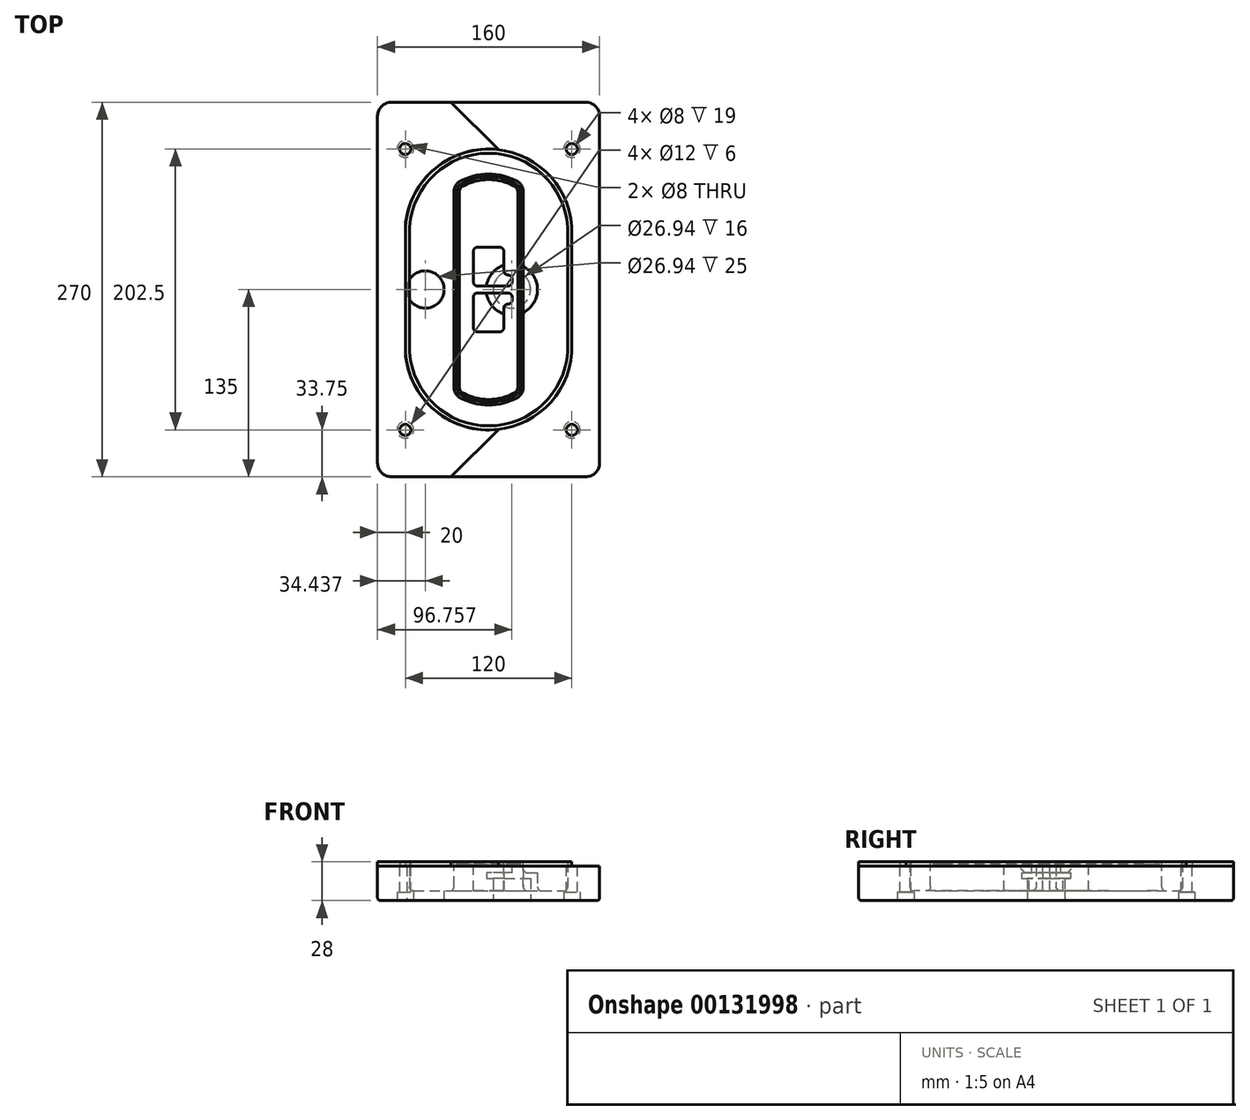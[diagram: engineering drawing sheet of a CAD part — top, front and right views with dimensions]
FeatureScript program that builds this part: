
annotation { "Feature Type Name" : "Feature", "Feature Type Description" : "" }
export const myFeature = defineFeature(function(context is Context, id is Id, definition is map)
    precondition{}
    {
        {
            var Q0;
            Q0=qCreatedBy(makeId("Top.planeOp"),FACE);
            var sketch = newSketch(context, id + "F0", { "sketchPlane" : qUnion([Q0])});
            skPoint(sketch, "E0.rect.middle", {"position": v(0, 0) * mm});
            skLineSegment(sketch, "E1.bottom", {"start": v(-70, -135) * mm, "end": v(70, -135) * mm});
            skLineSegment(sketch, "E1.top", {"start": v(-70, 135) * mm, "end": v(70, 135) * mm});
            skLineSegment(sketch, "E1.left", {"start": v(-80, -125) * mm, "end": v(-80, 125) * mm});
            skLineSegment(sketch, "E1.right", {"start": v(80, -125) * mm, "end": v(80, 125) * mm});
            skLineSegment(sketch, "E2", {"start": v(-80, 135) * mm, "end": v(80, -135) * mm, "construction": true});
            skLineSegment(sketch, "E3", {"start": v(80, 135) * mm, "end": v(-80, -135) * mm, "construction": true});
            skCircle(sketch, "E4", {"center": v(-60, 101.25) * mm, "radius": 4 * mm});
            skCircle(sketch, "E5", {"center": v(60, 101.25) * mm, "radius": 4 * mm});
            skCircle(sketch, "E6", {"center": v(60, -101.25) * mm, "radius": 4 * mm});
            skCircle(sketch, "E7", {"center": v(-60, -101.25) * mm, "radius": 4 * mm});
            skLineSegment(sketch, "E8", {"start": v(-60, 101.25) * mm, "end": v(60, 101.25) * mm, "construction": true});
            skLineSegment(sketch, "E9", {"start": v(60, 101.25) * mm, "end": v(60, -101.25) * mm, "construction": true});
            skLineSegment(sketch, "E10", {"start": v(60, -101.25) * mm, "end": v(-60, -101.25) * mm, "construction": true});
            skLineSegment(sketch, "E11", {"start": v(-60, -101.25) * mm, "end": v(-60, 101.25) * mm, "construction": true});
            skLineSegment(sketch, "E12", {"start": v(-60, 44.66) * mm, "end": v(-60, -44.66) * mm});
            skLineSegment(sketch, "E13", {"start": v(60, 44.66) * mm, "end": v(60, -44.66) * mm});
            skArc(sketch, "E14", {"start": v(59.98, 45.37) * mm, "mid": v(0, 101.25) * mm, "end": v(-59.98, 45.37) * mm});
            skArc(sketch, "E15", {"start": v(-59.98, -45.37) * mm, "mid": v(0, -101.25) * mm, "end": v(59.98, -45.37) * mm});
            skLineSegment(sketch, "E16", {"start": v(-60, 0) * mm, "end": v(60, 0) * mm, "construction": true});
            skPoint(sketch, "E17.visualSharp", {"position": v(-60, -45) * mm});
            skArc(sketch, "E17.filletArc", {"start": v(-60, -44.66) * mm, "mid": v(-60, -45.02) * mm, "end": v(-59.98, -45.37) * mm});
            skPoint(sketch, "E18.visualSharp", {"position": v(-60, 45) * mm});
            skArc(sketch, "E18.filletArc", {"start": v(-59.98, 45.37) * mm, "mid": v(-60, 45.02) * mm, "end": v(-60, 44.66) * mm});
            skPoint(sketch, "E19.visualSharp", {"position": v(60, 45) * mm});
            skArc(sketch, "E19.filletArc", {"start": v(60, 44.66) * mm, "mid": v(60, 45.02) * mm, "end": v(59.98, 45.37) * mm});
            skPoint(sketch, "E20.visualSharp", {"position": v(60, -45) * mm});
            skArc(sketch, "E20.filletArc", {"start": v(59.98, -45.37) * mm, "mid": v(60, -45.02) * mm, "end": v(60, -44.66) * mm});
            skPoint(sketch, "E21.visualSharp", {"position": v(-80, 135) * mm});
            skArc(sketch, "E21.filletArc", {"start": v(-70, 135) * mm, "mid": v(-77.07, 132.07) * mm, "end": v(-80, 125) * mm});
            skPoint(sketch, "E22.visualSharp", {"position": v(80, 135) * mm});
            skArc(sketch, "E22.filletArc", {"start": v(80, 125) * mm, "mid": v(77.07, 132.07) * mm, "end": v(70, 135) * mm});
            skPoint(sketch, "E23.visualSharp", {"position": v(80, -135) * mm});
            skArc(sketch, "E23.filletArc", {"start": v(70, -135) * mm, "mid": v(77.07, -132.07) * mm, "end": v(80, -125) * mm});
            skPoint(sketch, "E24.visualSharp", {"position": v(-80, -135) * mm});
            skArc(sketch, "E24.filletArc", {"start": v(-80, -125) * mm, "mid": v(-77.07, -132.07) * mm, "end": v(-70, -135) * mm});
            skArc(sketch, "E25.0", {"start": v(57, 44.66) * mm, "mid": v(57, 44.9) * mm, "end": v(56.98, 45.16) * mm});
            skLineSegment(sketch, "E25.1", {"start": v(57, 44.66) * mm, "end": v(57, -44.66) * mm});
            skArc(sketch, "E25.2", {"start": v(56.98, -45.16) * mm, "mid": v(57, -44.9) * mm, "end": v(57, -44.66) * mm});
            skArc(sketch, "E25.3", {"start": v(-56.98, -45.16) * mm, "mid": v(0, -98.25) * mm, "end": v(56.98, -45.16) * mm});
            skArc(sketch, "E25.4", {"start": v(-57, -44.66) * mm, "mid": v(-57, -44.9) * mm, "end": v(-56.98, -45.16) * mm});
            skArc(sketch, "E25.5", {"start": v(56.98, 45.16) * mm, "mid": v(0, 98.25) * mm, "end": v(-56.98, 45.16) * mm});
            skLineSegment(sketch, "E25.6", {"start": v(-57, 44.66) * mm, "end": v(-57, -44.66) * mm});
            skArc(sketch, "E25.7", {"start": v(-56.98, 45.16) * mm, "mid": v(-57, 44.9) * mm, "end": v(-57, 44.66) * mm});
            skArc(sketch, "E26.0", {"start": v(-63.97, 45.65) * mm, "mid": v(-64, 45.16) * mm, "end": v(-64, 44.66) * mm});
            skArc(sketch, "E26.1", {"start": v(63.97, 45.65) * mm, "mid": v(0, 105.25) * mm, "end": v(-63.97, 45.65) * mm});
            skArc(sketch, "E26.2", {"start": v(64, 44.66) * mm, "mid": v(64, 45.16) * mm, "end": v(63.97, 45.65) * mm});
            skLineSegment(sketch, "E26.3", {"start": v(64, 44.66) * mm, "end": v(64, -44.66) * mm});
            skArc(sketch, "E26.4", {"start": v(63.97, -45.65) * mm, "mid": v(64, -45.16) * mm, "end": v(64, -44.66) * mm});
            skLineSegment(sketch, "E26.5", {"start": v(-64, 44.66) * mm, "end": v(-64, -44.66) * mm});
            skArc(sketch, "E26.6", {"start": v(-63.97, -45.65) * mm, "mid": v(0, -105.25) * mm, "end": v(63.97, -45.65) * mm});
            skArc(sketch, "E26.7", {"start": v(-64, -44.66) * mm, "mid": v(-64, -45.16) * mm, "end": v(-63.97, -45.65) * mm});
            skSolve(sketch);
        }
        {
            var Q0;
            Q0=makeQuery(id+"F0.imprint","IMPRINT",FACE,{"disambiguationData":[TD([[makeQuery(id+"F0.imprint","IMPRINT",EDGE,{"derivedFrom":sQuery(id+"F0.wireOp",EDGE,"E1.bottom")}),1.0]])]});
            var Q1;
            Q1=makeQuery(id+"F0.imprint","IMPRINT",FACE,{"disambiguationData":[TD([[makeQuery(id+"F0.imprint","IMPRINT",EDGE,{"derivedFrom":sQuery(id+"F0.wireOp",EDGE,"E12")}),1.0]])]});
            var Q2;
            Q2=makeQuery(id+"F0.imprint","IMPRINT",FACE,{"disambiguationData":[TD([[makeQuery(id+"F0.imprint","IMPRINT",EDGE,{"derivedFrom":sQuery(id+"F0.wireOp",EDGE,"E25.0")}),1.0]])]});
            var Q3;
            Q3=makeQuery(id+"F0.imprint","IMPRINT",FACE,{"disambiguationData":[TD([[makeQuery(id+"F0.imprint","IMPRINT",EDGE,{"derivedFrom":sQuery(id+"F0.wireOp",EDGE,"E12")}),-1.0]])]});
            extrude(context, id + "F1", {"entities" : qUnion([Q0, Q1, Q2, Q3]), "oppositeDirection" : true, "depth" : 25 * mm});
        }
        {
            var Q0;
            Q0=makeQuery(id+"F0.imprint","IMPRINT",FACE,{"disambiguationData":[TD([[makeQuery(id+"F0.imprint","IMPRINT",EDGE,{"derivedFrom":sQuery(id+"F0.wireOp",EDGE,"E12")}),1.0]])]});
            extrude(context, id + "F2", {"entities" : qUnion([Q0]), "operationType" : NewBodyOperationType.ADD, "depth" : 3 * mm});
        }
        {
            var Q0;
            Q0=makeQuery(id+"F0.imprint","IMPRINT",FACE,{"disambiguationData":[TD([[makeQuery(id+"F0.imprint","IMPRINT",EDGE,{"derivedFrom":sQuery(id+"F0.wireOp",EDGE,"E25.0")}),1.0]])]});
            extrude(context, id + "F3", {"entities" : qUnion([Q0]), "operationType" : NewBodyOperationType.REMOVE, "oppositeDirection" : true, "depth" : 18 * mm});
        }
        {
            var Q0;
            Q0=makeQuery(id+"F2.opExtrude","CAP_FACE",FACE,{"disambiguationData":[OSD([sQuery(id+"F0.wireOp",EDGE,"E12"),sQuery(id+"F0.wireOp",EDGE,"E13"),sQuery(id+"F0.wireOp",EDGE,"E14"),sQuery(id+"F0.wireOp",EDGE,"E15"),sQuery(id+"F0.wireOp",EDGE,"E17.filletArc"),sQuery(id+"F0.wireOp",EDGE,"E18.filletArc"),sQuery(id+"F0.wireOp",EDGE,"E19.filletArc"),sQuery(id+"F0.wireOp",EDGE,"E20.filletArc"),sQuery(id+"F0.wireOp",EDGE,"E25.0"),sQuery(id+"F0.wireOp",EDGE,"E25.1"),sQuery(id+"F0.wireOp",EDGE,"E25.2"),sQuery(id+"F0.wireOp",EDGE,"E25.3"),sQuery(id+"F0.wireOp",EDGE,"E25.4"),sQuery(id+"F0.wireOp",EDGE,"E25.5"),sQuery(id+"F0.wireOp",EDGE,"E25.6"),sQuery(id+"F0.wireOp",EDGE,"E25.7")])],"isStart":false});
            var sketch = newSketch(context, id + "F4", { "sketchPlane" : qUnion([Q0])});
            skArc(sketch, "E27.0", {"start": v(-20.99, -77.65) * mm, "mid": v(0, -83.25) * mm, "end": v(20.99, -77.65) * mm});
            skArc(sketch, "E28.0", {"start": v(20.99, 77.65) * mm, "mid": v(0, 83.25) * mm, "end": v(-20.99, 77.65) * mm});
            skLineSegment(sketch, "E29", {"start": v(-25, 70.71) * mm, "end": v(-25, -70.71) * mm});
            skLineSegment(sketch, "E30", {"start": v(25, 70.71) * mm, "end": v(25, -70.71) * mm});
            skLineSegment(sketch, "E31", {"start": v(-25, 75.03) * mm, "end": v(25, 75.03) * mm, "construction": true});
            skLineSegment(sketch, "E32", {"start": v(-25, -75.03) * mm, "end": v(25, -75.03) * mm, "construction": true});
            skPoint(sketch, "E33.visualSharp", {"position": v(-25, 75.03) * mm});
            skArc(sketch, "E33.filletArc", {"start": v(-20.99, 77.65) * mm, "mid": v(-23.92, 74.72) * mm, "end": v(-25, 70.71) * mm});
            skPoint(sketch, "E34.visualSharp", {"position": v(25, 75.03) * mm});
            skArc(sketch, "E34.filletArc", {"start": v(25, 70.71) * mm, "mid": v(23.92, 74.72) * mm, "end": v(20.99, 77.65) * mm});
            skPoint(sketch, "E35.visualSharp", {"position": v(25, -75.03) * mm});
            skArc(sketch, "E35.filletArc", {"start": v(20.99, -77.65) * mm, "mid": v(23.92, -74.72) * mm, "end": v(25, -70.71) * mm});
            skPoint(sketch, "E36.visualSharp", {"position": v(-25, -75.03) * mm});
            skArc(sketch, "E36.filletArc", {"start": v(-25, -70.71) * mm, "mid": v(-23.92, -74.72) * mm, "end": v(-20.99, -77.65) * mm});
            skArc(sketch, "E37.0", {"start": v(56.98, 45.16) * mm, "mid": v(0, 98.25) * mm, "end": v(-56.98, 45.16) * mm});
            skArc(sketch, "E37.1", {"start": v(-56.98, 45.16) * mm, "mid": v(-57, 44.9) * mm, "end": v(-57, 44.66) * mm});
            skLineSegment(sketch, "E37.2", {"start": v(-57, 44.66) * mm, "end": v(-57, -44.66) * mm});
            skArc(sketch, "E37.3", {"start": v(-57, -44.66) * mm, "mid": v(-57, -44.9) * mm, "end": v(-56.98, -45.16) * mm});
            skArc(sketch, "E37.4", {"start": v(-56.98, -45.16) * mm, "mid": v(0, -98.25) * mm, "end": v(56.98, -45.16) * mm});
            skArc(sketch, "E37.5", {"start": v(56.98, -45.16) * mm, "mid": v(57, -44.9) * mm, "end": v(57, -44.66) * mm});
            skLineSegment(sketch, "E37.6", {"start": v(57, 44.66) * mm, "end": v(57, -44.66) * mm});
            skArc(sketch, "E37.7", {"start": v(57, 44.66) * mm, "mid": v(57, 44.9) * mm, "end": v(56.98, 45.16) * mm});
            skLineSegment(sketch, "E38.0", {"start": v(23, 70.71) * mm, "end": v(23, -70.71) * mm});
            skArc(sketch, "E38.1", {"start": v(19.99, -75.92) * mm, "mid": v(22.2, -73.72) * mm, "end": v(23, -70.71) * mm});
            skArc(sketch, "E38.2", {"start": v(-19.99, -75.92) * mm, "mid": v(0, -81.25) * mm, "end": v(19.99, -75.92) * mm});
            skArc(sketch, "E38.3", {"start": v(-23, -70.71) * mm, "mid": v(-22.2, -73.72) * mm, "end": v(-19.99, -75.92) * mm});
            skLineSegment(sketch, "E38.4", {"start": v(-23, 70.71) * mm, "end": v(-23, -70.71) * mm});
            skArc(sketch, "E38.5", {"start": v(23, 70.71) * mm, "mid": v(22.2, 73.72) * mm, "end": v(19.99, 75.92) * mm});
            skArc(sketch, "E38.6", {"start": v(-19.99, 75.92) * mm, "mid": v(-22.2, 73.72) * mm, "end": v(-23, 70.71) * mm});
            skArc(sketch, "E38.7", {"start": v(19.99, 75.92) * mm, "mid": v(0, 81.25) * mm, "end": v(-19.99, 75.92) * mm});
            skArc(sketch, "E39.0", {"start": v(21, 70.71) * mm, "mid": v(20.46, 72.72) * mm, "end": v(19, 74.18) * mm});
            skLineSegment(sketch, "E39.1", {"start": v(21, 70.71) * mm, "end": v(21, -70.71) * mm});
            skArc(sketch, "E39.2", {"start": v(19, -74.18) * mm, "mid": v(20.46, -72.72) * mm, "end": v(21, -70.71) * mm});
            skArc(sketch, "E39.3", {"start": v(-19, -74.18) * mm, "mid": v(0, -79.25) * mm, "end": v(19, -74.18) * mm});
            skArc(sketch, "E39.4", {"start": v(-21, -70.71) * mm, "mid": v(-20.46, -72.72) * mm, "end": v(-19, -74.18) * mm});
            skArc(sketch, "E39.5", {"start": v(19, 74.18) * mm, "mid": v(0, 79.25) * mm, "end": v(-19, 74.18) * mm});
            skLineSegment(sketch, "E39.6", {"start": v(-21, 70.71) * mm, "end": v(-21, -70.71) * mm});
            skArc(sketch, "E39.7", {"start": v(-19, 74.18) * mm, "mid": v(-20.46, 72.72) * mm, "end": v(-21, 70.71) * mm});
            skLineSegment(sketch, "E40", {"start": v(-25, 0) * mm, "end": v(25, 0) * mm, "construction": true});
            skLineSegment(sketch, "E41", {"start": v(-11, 5.5) * mm, "end": v(-11, 27.5) * mm});
            skLineSegment(sketch, "E42", {"start": v(-8, 30.5) * mm, "end": v(8, 30.5) * mm});
            skLineSegment(sketch, "E43", {"start": v(11, 27.5) * mm, "end": v(11, 13.5) * mm});
            skLineSegment(sketch, "E44", {"start": v(14, 10.5) * mm, "end": v(14, 10.5) * mm});
            skLineSegment(sketch, "E45", {"start": v(17, 7.5) * mm, "end": v(17, 5.5) * mm});
            skLineSegment(sketch, "E46", {"start": v(14, 2.5) * mm, "end": v(-8, 2.5) * mm});
            skPoint(sketch, "E47.visualSharp", {"position": v(-11, 30.5) * mm});
            skArc(sketch, "E47.filletArc", {"start": v(-8, 30.5) * mm, "mid": v(-10.12, 29.62) * mm, "end": v(-11, 27.5) * mm});
            skPoint(sketch, "E48.visualSharp", {"position": v(11, 30.5) * mm});
            skArc(sketch, "E48.filletArc", {"start": v(11, 27.5) * mm, "mid": v(10.12, 29.62) * mm, "end": v(8, 30.5) * mm});
            skPoint(sketch, "E49.visualSharp", {"position": v(11, 10.5) * mm});
            skArc(sketch, "E49.filletArc", {"start": v(11, 13.5) * mm, "mid": v(11.88, 11.38) * mm, "end": v(14, 10.5) * mm});
            skPoint(sketch, "E50.visualSharp", {"position": v(17, 10.5) * mm});
            skArc(sketch, "E50.filletArc", {"start": v(17, 7.5) * mm, "mid": v(16.12, 9.62) * mm, "end": v(14, 10.5) * mm});
            skPoint(sketch, "E51.visualSharp", {"position": v(17, 2.5) * mm});
            skArc(sketch, "E51.filletArc", {"start": v(14, 2.5) * mm, "mid": v(16.12, 3.38) * mm, "end": v(17, 5.5) * mm});
            skPoint(sketch, "E52.visualSharp", {"position": v(-11, 2.5) * mm});
            skArc(sketch, "E52.filletArc", {"start": v(-11, 5.5) * mm, "mid": v(-10.12, 3.38) * mm, "end": v(-8, 2.5) * mm});
            skLineSegment(sketch, "E53.0.MirrorCS", {"start": v(14, -2.5) * mm, "end": v(-8, -2.5) * mm});
            skArc(sketch, "E54.0.MirrorCS", {"start": v(-11, -5.5) * mm, "mid": v(-10.12, -3.38) * mm, "end": v(-8, -2.5) * mm});
            skLineSegment(sketch, "E55.0.MirrorCS", {"start": v(-11, -5.5) * mm, "end": v(-11, -27.5) * mm});
            skArc(sketch, "E56.0.MirrorCS", {"start": v(-8, -30.5) * mm, "mid": v(-10.12, -29.62) * mm, "end": v(-11, -27.5) * mm});
            skLineSegment(sketch, "E57.0.MirrorCS", {"start": v(-8, -30.5) * mm, "end": v(8, -30.5) * mm});
            skArc(sketch, "E58.0.MirrorCS", {"start": v(11, -27.5) * mm, "mid": v(10.12, -29.62) * mm, "end": v(8, -30.5) * mm});
            skLineSegment(sketch, "E59.0.MirrorCS", {"start": v(11, -27.5) * mm, "end": v(11, -13.5) * mm});
            skArc(sketch, "E60.0.MirrorCS", {"start": v(11, -13.5) * mm, "mid": v(11.88, -11.38) * mm, "end": v(14, -10.5) * mm});
            skArc(sketch, "E61.0.MirrorCS", {"start": v(17, -7.5) * mm, "mid": v(16.12, -9.62) * mm, "end": v(14, -10.5) * mm});
            skLineSegment(sketch, "E62.0.MirrorCS", {"start": v(17, -7.5) * mm, "end": v(17, -5.5) * mm});
            skArc(sketch, "E63.0.MirrorCS", {"start": v(14, -2.5) * mm, "mid": v(16.12, -3.38) * mm, "end": v(17, -5.5) * mm});
            skSolve(sketch);
        }
        {
            var Q0;
            Q0=makeQuery(id+"F4.imprint","IMPRINT",FACE,{"disambiguationData":[TD([[makeQuery(id+"F4.imprint","IMPRINT",EDGE,{"derivedFrom":sQuery(id+"F4.wireOp",EDGE,"E27.0")}),1.0]])]});
            var Q1;
            Q1=makeQuery(id+"F4.imprint","IMPRINT",FACE,{"disambiguationData":[TD([[makeQuery(id+"F4.imprint","IMPRINT",EDGE,{"derivedFrom":sQuery(id+"F4.wireOp",EDGE,"E38.0")}),-1.0]])]});
            var Q2;
            Q2=makeQuery(id+"F4.imprint","IMPRINT",FACE,{"disambiguationData":[TD([[makeQuery(id+"F4.imprint","IMPRINT",EDGE,{"derivedFrom":sQuery(id+"F4.wireOp",EDGE,"E39.0")}),1.0]])]});
            extrude(context, id + "F5", {"entities" : qUnion([Q0, Q1, Q2]), "operationType" : NewBodyOperationType.ADD, "endBound" : BoundingType.UP_TO_NEXT, "oppositeDirection" : true, "depth" : 25 * mm});
        }
        {
            var Q0;
            Q0=makeQuery(id+"F4.imprint","IMPRINT",FACE,{"disambiguationData":[TD([[makeQuery(id+"F4.imprint","IMPRINT",EDGE,{"derivedFrom":sQuery(id+"F4.wireOp",EDGE,"E38.0")}),-1.0]])]});
            extrude(context, id + "F6", {"entities" : qUnion([Q0]), "operationType" : NewBodyOperationType.REMOVE, "oppositeDirection" : true, "depth" : 2 * mm});
        }
        {
            var Q0;
            Q0=makeQuery(id+"F1.opExtrude","CAP_FACE",FACE,{"disambiguationData":[OSD([sQuery(id+"F0.wireOp",EDGE,"E1.bottom"),sQuery(id+"F0.wireOp",EDGE,"E1.top"),sQuery(id+"F0.wireOp",EDGE,"E1.left"),sQuery(id+"F0.wireOp",EDGE,"E1.right"),sQuery(id+"F0.wireOp",EDGE,"E4"),sQuery(id+"F0.wireOp",EDGE,"E5"),sQuery(id+"F0.wireOp",EDGE,"E6"),sQuery(id+"F0.wireOp",EDGE,"E7"),sQuery(id+"F0.wireOp",EDGE,"E21.filletArc"),sQuery(id+"F0.wireOp",EDGE,"E22.filletArc"),sQuery(id+"F0.wireOp",EDGE,"E23.filletArc"),sQuery(id+"F0.wireOp",EDGE,"E24.filletArc")])],"isStart":false});
            var sketch = newSketch(context, id + "F7", { "sketchPlane" : qUnion([Q0])});
            skCircle(sketch, "E64", {"center": v(16.76, 0) * mm, "radius": 13.47 * mm});
            skCircle(sketch, "E65", {"center": v(-45.56, 0) * mm, "radius": 13.47 * mm});
            skLineSegment(sketch, "E66", {"start": v(80, 0) * mm, "end": v(-80, 0) * mm});
            skCircle(sketch, "E67", {"center": v(16.76, 0) * mm, "radius": 18.47 * mm});
            skCircle(sketch, "E68", {"center": v(60, -101.25) * mm, "radius": 6 * mm});
            skCircle(sketch, "E69", {"center": v(-60, -101.25) * mm, "radius": 6 * mm});
            skCircle(sketch, "E70", {"center": v(-60, 101.25) * mm, "radius": 6 * mm});
            skCircle(sketch, "E71", {"center": v(60, 101.25) * mm, "radius": 6 * mm});
            skSolve(sketch);
        }
        {
            var Q0;
            {var subQ1=sQuery(id+"F7.wireOp",EDGE,"E66");var subQ4=sQuery(id+"F7.wireOp",EDGE,"E64");var subQ6=makeQuery(id+"F7.imprint","INTERSECT",VERTEX,{"disambiguationData":[OD(0.0)],"derivedFrom":[subQ4,subQ1]});Q0=makeQuery(id+"F7.imprint","IMPRINT",FACE,{"disambiguationData":[TD([[makeQuery(id+"F7.imprint","IMPRINT",EDGE,{"disambiguationData":[TD([[subQ6,-1.0]])],"derivedFrom":subQ4}),-1.0]])]});}
            var Q1;
            {var subQ0=sQuery(id+"F7.wireOp",EDGE,"E66");var subQ1=sQuery(id+"F7.wireOp",EDGE,"E64");var subQ3=makeQuery(id+"F7.imprint","INTERSECT",VERTEX,{"disambiguationData":[OD(0.0)],"derivedFrom":[subQ1,subQ0]});Q1=makeQuery(id+"F7.imprint","IMPRINT",FACE,{"disambiguationData":[TD([[makeQuery(id+"F7.imprint","IMPRINT",EDGE,{"disambiguationData":[TD([[subQ3,-1.0]])],"derivedFrom":subQ1}),1.0]])]});}
            var Q2;
            {var subQ0=sQuery(id+"F7.wireOp",EDGE,"E66");var subQ1=sQuery(id+"F7.wireOp",EDGE,"E64");var subQ3=makeQuery(id+"F7.imprint","INTERSECT",VERTEX,{"disambiguationData":[OD(0.0)],"derivedFrom":[subQ1,subQ0]});Q2=makeQuery(id+"F7.imprint","IMPRINT",FACE,{"disambiguationData":[TD([[makeQuery(id+"F7.imprint","IMPRINT",EDGE,{"disambiguationData":[TD([[subQ3,1.0]])],"derivedFrom":subQ1}),1.0]])]});}
            var Q3;
            {var subQ1=sQuery(id+"F7.wireOp",EDGE,"E66");var subQ4=sQuery(id+"F7.wireOp",EDGE,"E64");var subQ6=makeQuery(id+"F7.imprint","INTERSECT",VERTEX,{"disambiguationData":[OD(0.0)],"derivedFrom":[subQ4,subQ1]});Q3=makeQuery(id+"F7.imprint","IMPRINT",FACE,{"disambiguationData":[TD([[makeQuery(id+"F7.imprint","IMPRINT",EDGE,{"disambiguationData":[TD([[subQ6,1.0]])],"derivedFrom":subQ4}),-1.0]])]});}
            extrude(context, id + "F8", {"entities" : qUnion([Q0, Q1, Q2, Q3]), "operationType" : NewBodyOperationType.ADD, "oppositeDirection" : true, "depth" : 20 * mm});
        }
        {
            var Q0;
            {var subQ0=sQuery(id+"F7.wireOp",EDGE,"E66");var subQ1=sQuery(id+"F7.wireOp",EDGE,"E64");var subQ3=makeQuery(id+"F7.imprint","INTERSECT",VERTEX,{"disambiguationData":[OD(0.0)],"derivedFrom":[subQ1,subQ0]});Q0=makeQuery(id+"F7.imprint","IMPRINT",FACE,{"disambiguationData":[TD([[makeQuery(id+"F7.imprint","IMPRINT",EDGE,{"disambiguationData":[TD([[subQ3,-1.0]])],"derivedFrom":subQ1}),1.0]])]});}
            var Q1;
            {var subQ0=sQuery(id+"F7.wireOp",EDGE,"E66");var subQ1=sQuery(id+"F7.wireOp",EDGE,"E64");var subQ3=makeQuery(id+"F7.imprint","INTERSECT",VERTEX,{"disambiguationData":[OD(0.0)],"derivedFrom":[subQ1,subQ0]});Q1=makeQuery(id+"F7.imprint","IMPRINT",FACE,{"disambiguationData":[TD([[makeQuery(id+"F7.imprint","IMPRINT",EDGE,{"disambiguationData":[TD([[subQ3,1.0]])],"derivedFrom":subQ1}),1.0]])]});}
            extrude(context, id + "F9", {"entities" : qUnion([Q0, Q1]), "operationType" : NewBodyOperationType.REMOVE, "oppositeDirection" : true, "depth" : 16 * mm});
        }
        {
            var Q0;
            {var subQ0=sQuery(id+"F7.wireOp",EDGE,"E66");var subQ1=sQuery(id+"F7.wireOp",EDGE,"E65");var subQ3=makeQuery(id+"F7.imprint","INTERSECT",VERTEX,{"disambiguationData":[OD(0.0)],"derivedFrom":[subQ1,subQ0]});Q0=makeQuery(id+"F7.imprint","IMPRINT",FACE,{"disambiguationData":[TD([[makeQuery(id+"F7.imprint","IMPRINT",EDGE,{"disambiguationData":[TD([[subQ3,-1.0]])],"derivedFrom":subQ1}),1.0]])]});}
            var Q1;
            {var subQ0=sQuery(id+"F7.wireOp",EDGE,"E66");var subQ1=sQuery(id+"F7.wireOp",EDGE,"E65");var subQ3=makeQuery(id+"F7.imprint","INTERSECT",VERTEX,{"disambiguationData":[OD(0.0)],"derivedFrom":[subQ1,subQ0]});Q1=makeQuery(id+"F7.imprint","IMPRINT",FACE,{"disambiguationData":[TD([[makeQuery(id+"F7.imprint","IMPRINT",EDGE,{"disambiguationData":[TD([[subQ3,1.0]])],"derivedFrom":subQ1}),1.0]])]});}
            extrude(context, id + "F10", {"entities" : qUnion([Q0, Q1]), "operationType" : NewBodyOperationType.REMOVE, "oppositeDirection" : true, "depth" : 25 * mm});
        }
        {
            var Q0;
            Q0=makeQuery(id+"F7.imprint","IMPRINT",FACE,{"disambiguationData":[TD([[makeQuery(id+"F7.imprint","IMPRINT",EDGE,{"derivedFrom":sQuery(id+"F7.wireOp",EDGE,"E68")}),1.0]])]});
            var Q1;
            Q1=makeQuery(id+"F7.imprint","IMPRINT",FACE,{"disambiguationData":[TD([[makeQuery(id+"F7.imprint","IMPRINT",EDGE,{"derivedFrom":makeQuery(id+"F1.opExtrude","CAP_EDGE",EDGE,{"disambiguationData":[OSD([sQuery(id+"F0.wireOp",EDGE,"E5")])],"isStart":false})}),-1.0]])]});
            var Q2;
            Q2=makeQuery(id+"F7.imprint","IMPRINT",FACE,{"disambiguationData":[TD([[makeQuery(id+"F7.imprint","IMPRINT",EDGE,{"derivedFrom":sQuery(id+"F7.wireOp",EDGE,"E69")}),1.0]])]});
            var Q3;
            Q3=makeQuery(id+"F7.imprint","IMPRINT",FACE,{"disambiguationData":[TD([[makeQuery(id+"F7.imprint","IMPRINT",EDGE,{"derivedFrom":makeQuery(id+"F1.opExtrude","CAP_EDGE",EDGE,{"disambiguationData":[OSD([sQuery(id+"F0.wireOp",EDGE,"E4")])],"isStart":false})}),-1.0]])]});
            var Q4;
            Q4=makeQuery(id+"F7.imprint","IMPRINT",FACE,{"disambiguationData":[TD([[makeQuery(id+"F7.imprint","IMPRINT",EDGE,{"derivedFrom":sQuery(id+"F7.wireOp",EDGE,"E70")}),1.0]])]});
            var Q5;
            Q5=makeQuery(id+"F7.imprint","IMPRINT",FACE,{"disambiguationData":[TD([[makeQuery(id+"F7.imprint","IMPRINT",EDGE,{"derivedFrom":makeQuery(id+"F1.opExtrude","CAP_EDGE",EDGE,{"disambiguationData":[OSD([sQuery(id+"F0.wireOp",EDGE,"E7")])],"isStart":false})}),-1.0]])]});
            var Q6;
            Q6=makeQuery(id+"F7.imprint","IMPRINT",FACE,{"disambiguationData":[TD([[makeQuery(id+"F7.imprint","IMPRINT",EDGE,{"derivedFrom":sQuery(id+"F7.wireOp",EDGE,"E71")}),1.0]])]});
            var Q7;
            Q7=makeQuery(id+"F7.imprint","IMPRINT",FACE,{"disambiguationData":[TD([[makeQuery(id+"F7.imprint","IMPRINT",EDGE,{"derivedFrom":makeQuery(id+"F1.opExtrude","CAP_EDGE",EDGE,{"disambiguationData":[OSD([sQuery(id+"F0.wireOp",EDGE,"E6")])],"isStart":false})}),-1.0]])]});
            extrude(context, id + "F11", {"entities" : qUnion([Q0, Q1, Q2, Q3, Q4, Q5, Q6, Q7]), "operationType" : NewBodyOperationType.REMOVE, "oppositeDirection" : true, "depth" : 6 * mm});
        }
        {
            var Q0;
            Q0=makeQuery(id+"F9.boolean.opBoolean","COPY",FACE,{"derivedFrom":makeQuery(id+"F9.opExtrude","CAP_FACE",FACE,{"disambiguationData":[OSD([sQuery(id+"F7.wireOp",EDGE,"E64")])],"isStart":false})});
            var sketch = newSketch(context, id + "F12", { "sketchPlane" : qUnion([Q0])});
            skArc(sketch, "E72.0", {"start": v(11, 17.55) * mm, "mid": v(2.57, 11.82) * mm, "end": v(-1.54, 2.5) * mm});
            skArc(sketch, "E72.1", {"start": v(-1.54, -2.5) * mm, "mid": v(2.57, -11.82) * mm, "end": v(11, -17.55) * mm});
            skLineSegment(sketch, "E73", {"start": v(-1.54, -2.5) * mm, "end": v(14, -2.5) * mm});
            skLineSegment(sketch, "E74.0", {"start": v(14, 2.5) * mm, "end": v(-1.54, 2.5) * mm});
            skArc(sketch, "E74.1", {"start": v(14, 2.5) * mm, "mid": v(16.12, 3.38) * mm, "end": v(17, 5.5) * mm});
            skLineSegment(sketch, "E74.2", {"start": v(17, 7.5) * mm, "end": v(17, 5.5) * mm});
            skArc(sketch, "E74.3", {"start": v(17, 7.5) * mm, "mid": v(16.12, 9.62) * mm, "end": v(14, 10.5) * mm});
            skArc(sketch, "E74.4", {"start": v(11, 13.5) * mm, "mid": v(11.88, 11.38) * mm, "end": v(14, 10.5) * mm});
            skLineSegment(sketch, "E74.5", {"start": v(11, 17.55) * mm, "end": v(11, 13.5) * mm});
            skLineSegment(sketch, "E74.7", {"start": v(14, -2.5) * mm, "end": v(-1.54, -2.5) * mm});
            skArc(sketch, "E74.8", {"start": v(14, -2.5) * mm, "mid": v(16.12, -3.38) * mm, "end": v(17, -5.5) * mm});
            skLineSegment(sketch, "E74.9", {"start": v(17, -7.5) * mm, "end": v(17, -5.5) * mm});
            skArc(sketch, "E74.10", {"start": v(17, -7.5) * mm, "mid": v(16.12, -9.62) * mm, "end": v(14, -10.5) * mm});
            skArc(sketch, "E74.11", {"start": v(11, -13.5) * mm, "mid": v(11.88, -11.38) * mm, "end": v(14, -10.5) * mm});
            skLineSegment(sketch, "E74.12", {"start": v(11, -17.55) * mm, "end": v(11, -13.5) * mm});
            skPoint(sketch, "E75.orphan", {"position": v(11, -27.5) * mm});
            skPoint(sketch, "E76.orphan", {"position": v(-8, -2.5) * mm});
            skPoint(sketch, "E77.orphan", {"position": v(-8, 2.5) * mm});
            skPoint(sketch, "E78.orphan", {"position": v(11, 27.5) * mm});
            skSolve(sketch);
        }
        {
            var Q0;
            {var subQ7=sQuery(id+"F12.wireOp",EDGE,"E72.0");var subQ14=sQuery(id+"F12.wireOp",EDGE,"E72.1");var subQ16=sQuery(id+"F12.wireOp",EDGE,"E74.1");var subQ18=sQuery(id+"F12.wireOp",EDGE,"E74.8");Q0=qUnion([makeQuery(id+"F12.imprint","IMPRINT",FACE,{"disambiguationData":[TD([[makeQuery(id+"F12.imprint","IMPRINT",EDGE,{"derivedFrom":subQ7}),1.0]])]}),makeQuery(id+"F12.imprint","IMPRINT",FACE,{"disambiguationData":[TD([[makeQuery(id+"F12.imprint","IMPRINT",EDGE,{"derivedFrom":subQ14}),1.0]])]}),makeQuery(id+"F12.imprint","IMPRINT",FACE,{"disambiguationData":[TD([[makeQuery(id+"F12.imprint","IMPRINT",EDGE,{"derivedFrom":subQ16}),1.0]])]}),makeQuery(id+"F12.imprint","IMPRINT",FACE,{"disambiguationData":[TD([[makeQuery(id+"F12.imprint","IMPRINT",EDGE,{"derivedFrom":subQ18}),-1.0]])]})]);}
            var Q1;
            Q1=makeQuery(id+"F5.boolean.opBoolean","SPLIT",FACE,{"disambiguationData":[TD([makeQuery(id+"F5.opExtrude","SWEPT_FACE",FACE,{"disambiguationData":[OSD([sQuery(id+"F4.wireOp",EDGE,"E41")])]})])],"derivedFrom":makeQuery(id+"F3.boolean.opBoolean","COPY",FACE,{"derivedFrom":makeQuery(id+"F3.opExtrude","CAP_FACE",FACE,{"disambiguationData":[OSD([sQuery(id+"F0.wireOp",EDGE,"E25.0"),sQuery(id+"F0.wireOp",EDGE,"E25.1"),sQuery(id+"F0.wireOp",EDGE,"E25.2"),sQuery(id+"F0.wireOp",EDGE,"E25.3"),sQuery(id+"F0.wireOp",EDGE,"E25.4"),sQuery(id+"F0.wireOp",EDGE,"E25.5"),sQuery(id+"F0.wireOp",EDGE,"E25.6"),sQuery(id+"F0.wireOp",EDGE,"E25.7")])],"isStart":false})})});
            extrude(context, id + "F13", {"entities" : qUnion([Q0]), "operationType" : NewBodyOperationType.REMOVE, "endBound" : BoundingType.UP_TO_SURFACE, "endBoundEntityFace" : qUnion([Q1]), "depth" : 25 * mm});
        }
        {
            var Q0;
            Q0=makeQuery(id+"F3.boolean.opBoolean","COPY",EDGE,{"derivedFrom":makeQuery(id+"F3.opExtrude","CAP_EDGE",EDGE,{"disambiguationData":[OSD([sQuery(id+"F0.wireOp",EDGE,"E25.6")])],"isStart":false})});
            var Q1;
            Q1=makeQuery(id+"F8.boolean.opBoolean","INTERSECT",EDGE,{"derivedFrom":[makeQuery(id+"F5.opExtrude","SWEPT_FACE",FACE,{"disambiguationData":[OSD([sQuery(id+"F4.wireOp",EDGE,"E30")])]}),makeQuery(id+"F8.opExtrude","CAP_FACE",FACE,{"disambiguationData":[OSD([sQuery(id+"F7.wireOp",EDGE,"E67")])],"isStart":false})]});
            var Q2;
            Q2=makeQuery(id+"F8.boolean.opBoolean","INTERSECT",EDGE,{"disambiguationData":[OD(1.0)],"derivedFrom":[makeQuery(id+"F5.opExtrude","SWEPT_FACE",FACE,{"disambiguationData":[OSD([sQuery(id+"F4.wireOp",EDGE,"E30")])]}),makeQuery(id+"F8.opExtrude","SWEPT_FACE",FACE,{"disambiguationData":[OSD([sQuery(id+"F7.wireOp",EDGE,"E67")])]})]});
            var Q3;
            {var subQ0=sQuery(id+"F4.wireOp",EDGE,"E30");Q3=makeQuery(id+"F8.boolean.opBoolean","SPLIT",EDGE,{"disambiguationData":[TD([makeQuery(id+"F5.opExtrude","SWEPT_FACE",FACE,{"disambiguationData":[OSD([sQuery(id+"F4.wireOp",EDGE,"E35.filletArc")])]})])],"derivedFrom":makeQuery(id+"F5.opExtrude","CAP_EDGE",EDGE,{"disambiguationData":[OSD([subQ0])],"isStart":false})});}
            var Q4;
            {var subQ0=sQuery(id+"F0.wireOp",EDGE,"E25.7");var subQ1=sQuery(id+"F0.wireOp",EDGE,"E25.1");var subQ2=sQuery(id+"F0.wireOp",EDGE,"E25.6");var subQ3=sQuery(id+"F0.wireOp",EDGE,"E25.5");var subQ4=sQuery(id+"F0.wireOp",EDGE,"E25.4");var subQ5=sQuery(id+"F0.wireOp",EDGE,"E25.0");var subQ6=sQuery(id+"F0.wireOp",EDGE,"E25.2");var subQ7=sQuery(id+"F0.wireOp",EDGE,"E25.3");Q4=makeQuery(id+"F8.boolean.opBoolean","INTERSECT",EDGE,{"derivedFrom":[makeQuery(id+"F5.boolean.opBoolean","SPLIT",FACE,{"disambiguationData":[TD([makeQuery(id+"F2.opExtrude","SWEPT_FACE",FACE,{"disambiguationData":[OSD([subQ5])]})])],"derivedFrom":makeQuery(id+"F3.boolean.opBoolean","COPY",FACE,{"derivedFrom":makeQuery(id+"F3.opExtrude","CAP_FACE",FACE,{"disambiguationData":[OSD([subQ5,subQ1,subQ6,subQ7,subQ4,subQ3,subQ2,subQ0])],"isStart":false})})}),makeQuery(id+"F8.opExtrude","SWEPT_FACE",FACE,{"disambiguationData":[OSD([sQuery(id+"F7.wireOp",EDGE,"E67")])]})]});}
            var Q5;
            Q5=makeQuery(id+"F8.boolean.opBoolean","INTERSECT",EDGE,{"disambiguationData":[OD(0.0)],"derivedFrom":[makeQuery(id+"F5.opExtrude","SWEPT_FACE",FACE,{"disambiguationData":[OSD([sQuery(id+"F4.wireOp",EDGE,"E30")])]}),makeQuery(id+"F8.opExtrude","SWEPT_FACE",FACE,{"disambiguationData":[OSD([sQuery(id+"F7.wireOp",EDGE,"E67")])]})]});
            fillet(context, id + "F14", {"entities" : qUnion([Q0, Q1, Q2, Q3, Q4, Q5]), "radius" : 3 * mm, "tangentPropagation" : true, "allowEdgeOverflow" : false});
        }
        {
            var Q0;
            Q0=makeQuery(id+"F1.opExtrude","CAP_EDGE",EDGE,{"disambiguationData":[OSD([sQuery(id+"F0.wireOp",EDGE,"E1.bottom")])],"isStart":false});
            fillet(context, id + "F15", {"entities" : qUnion([Q0]), "radius" : 2 * mm, "tangentPropagation" : true, "allowEdgeOverflow" : false});
        }
        {
            var Q0;
            {var subQ0=sQuery(id+"F0.wireOp",EDGE,"E22.filletArc");var subQ1=sQuery(id+"F0.wireOp",EDGE,"E7");var subQ2=sQuery(id+"F0.wireOp",EDGE,"E6");var subQ3=sQuery(id+"F0.wireOp",EDGE,"E5");var subQ4=sQuery(id+"F0.wireOp",EDGE,"E4");var subQ5=sQuery(id+"F0.wireOp",EDGE,"E1.bottom");var subQ6=sQuery(id+"F0.wireOp",EDGE,"E21.filletArc");var subQ7=sQuery(id+"F0.wireOp",EDGE,"E1.top");var subQ8=sQuery(id+"F0.wireOp",EDGE,"E1.left");var subQ9=sQuery(id+"F0.wireOp",EDGE,"E1.right");var subQ10=sQuery(id+"F0.wireOp",EDGE,"E23.filletArc");var subQ11=sQuery(id+"F0.wireOp",EDGE,"E24.filletArc");Q0=makeQuery(id+"F2.boolean.opBoolean","SPLIT",FACE,{"disambiguationData":[TD([makeQuery(id+"F1.opExtrude","SWEPT_FACE",FACE,{"disambiguationData":[OSD([subQ5])]})])],"derivedFrom":makeQuery(id+"F1.opExtrude","CAP_FACE",FACE,{"disambiguationData":[OSD([subQ5,subQ7,subQ8,subQ9,subQ4,subQ3,subQ2,subQ1,subQ6,subQ0,subQ10,subQ11])],"isStart":true})});}
            var sketch = newSketch(context, id + "F16", { "sketchPlane" : qUnion([Q0])});
            skLineSegment(sketch, "E79", {"start": v(-71.82, 135) * mm, "end": v(-15, 153) * mm});
            skLineSegment(sketch, "E80", {"start": v(-15, 153) * mm, "end": v(-15, 165) * mm});
            skLineSegment(sketch, "E81", {"start": v(15, 92.86) * mm, "end": v(-27.14, 135) * mm});
            skLineSegment(sketch, "E82", {"start": v(15, 92.86) * mm, "end": v(15, 165) * mm});
            skCircle(sketch, "E83", {"center": v(0, 165) * mm, "radius": 6 * mm});
            skArc(sketch, "E84", {"start": v(15, 165) * mm, "mid": v(0, 180) * mm, "end": v(-15, 165) * mm});
            skLineSegment(sketch, "E85", {"start": v(0, 165) * mm, "end": v(0, 135) * mm, "construction": true});
            skLineSegment(sketch, "E86", {"start": v(-80, 0) * mm, "end": v(80, 0) * mm, "construction": true});
            skLineSegment(sketch, "E87.MirrorCS", {"start": v(0, -165) * mm, "end": v(0, -135) * mm, "construction": true});
            skLineSegment(sketch, "E88.MirrorCS", {"start": v(-71.82, -135) * mm, "end": v(-15, -153) * mm});
            skLineSegment(sketch, "E89.MirrorCS", {"start": v(15, -92.86) * mm, "end": v(-27.14, -135) * mm});
            skLineSegment(sketch, "E90.MirrorCS", {"start": v(15, -92.86) * mm, "end": v(15, -165) * mm});
            skArc(sketch, "E91.MirrorCS", {"start": v(15, -165) * mm, "mid": v(0, -180) * mm, "end": v(-15, -165) * mm});
            skCircle(sketch, "E92.MirrorC", {"center": v(0, -165) * mm, "radius": 6 * mm});
            skLineSegment(sketch, "E93.MirrorCS", {"start": v(-15, -153) * mm, "end": v(-15, -165) * mm});
            skSolve(sketch);
        }
        {
            var Q0;
            {var subQ1=sQuery(id+"F16.wireOp",EDGE,"E79");Q0=makeQuery(id+"F16.imprint","IMPRINT",FACE,{"disambiguationData":[TD([[makeQuery(id+"F16.imprint","IMPRINT",EDGE,{"derivedFrom":subQ1}),-1.0]])]});}
            var Q1;
            Q1=makeQuery(id+"F16.imprint","IMPRINT",FACE,{"disambiguationData":[TD([[makeQuery(id+"F16.imprint","IMPRINT",EDGE,{"derivedFrom":makeQuery(id+"F1.opExtrude","CAP_EDGE",EDGE,{"disambiguationData":[OSD([sQuery(id+"F0.wireOp",EDGE,"E1.left")])],"isStart":true})}),-1.0]])]});
            var Q2;
            {var subQ0=sQuery(id+"F16.wireOp",EDGE,"E88.MirrorCS");Q2=makeQuery(id+"F16.imprint","IMPRINT",FACE,{"disambiguationData":[TD([[makeQuery(id+"F16.imprint","IMPRINT",EDGE,{"derivedFrom":subQ0}),1.0]])]});}
            var Q3;
            Q3=makeQuery(id+"F2.opExtrude","CAP_FACE",FACE,{"disambiguationData":[OSD([sQuery(id+"F0.wireOp",EDGE,"E12"),sQuery(id+"F0.wireOp",EDGE,"E13"),sQuery(id+"F0.wireOp",EDGE,"E14"),sQuery(id+"F0.wireOp",EDGE,"E15"),sQuery(id+"F0.wireOp",EDGE,"E17.filletArc"),sQuery(id+"F0.wireOp",EDGE,"E18.filletArc"),sQuery(id+"F0.wireOp",EDGE,"E19.filletArc"),sQuery(id+"F0.wireOp",EDGE,"E20.filletArc"),sQuery(id+"F0.wireOp",EDGE,"E25.0"),sQuery(id+"F0.wireOp",EDGE,"E25.1"),sQuery(id+"F0.wireOp",EDGE,"E25.2"),sQuery(id+"F0.wireOp",EDGE,"E25.3"),sQuery(id+"F0.wireOp",EDGE,"E25.4"),sQuery(id+"F0.wireOp",EDGE,"E25.5"),sQuery(id+"F0.wireOp",EDGE,"E25.6"),sQuery(id+"F0.wireOp",EDGE,"E25.7")])],"isStart":false});
            extrude(context, id + "F17", {"entities" : qUnion([Q0, Q1, Q2]), "endBound" : BoundingType.UP_TO_SURFACE, "endBoundEntityFace" : qUnion([Q3]), "depth" : 25 * mm});
        }
    });
